# Revit family: Holyoake_-_PRD_Pressure Relief Damper Duct Flange
name_source: partatom
category: Duct Accessories
revit_build: Autodesk Revit 2014 (Build: 20130308_1515(x64)
units: mm (PartAtom-declared; Revit-internal decimal feet)

## types (1)
- Holyoake_-_PRD_Pressure Relief Damper Duct Flange
    Blade Angle = 65.00°
    Duct Flange H = 35 mm  [stored 0.114829 ft]
    Duct Flange W = 155 mm  [stored 0.50853 ft]
    H = 834 mm  [stored 2.73622 ft]
    Manufacturer = Holyoake Industries Ltd.
    Material = Aluminium
    Maximum Height = 1494 mm  [stored 4.90157 ft]
    Maximum Width = 750 mm  [stored 2.46063 ft]
    Minimum Height = 180 mm  [stored 0.590551 ft]
    Minimum Width = 150 mm
    Model = PRD150 Duct Flange
    Nominal H = 764 mm  [stored 2.50656 ft]
    Nominal W = 600 mm
    Parametric H = 800 mm  [stored 2.62467 ft]
    Parametric W = 600 mm
    URL = http://www.productspec.net
    W = 670 mm

note: [stored X ft] marks values corroborated as IEEE doubles in the binary element streams (Revit-internal decimal feet)

## geometry (parser evidence)
native form markers: Sweep x15
no freeform markers — native parametric forms only
